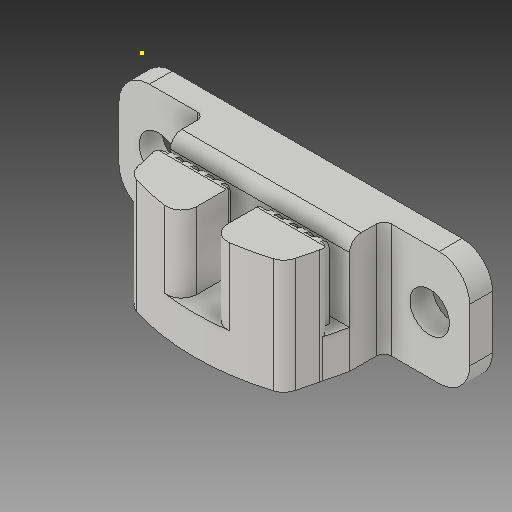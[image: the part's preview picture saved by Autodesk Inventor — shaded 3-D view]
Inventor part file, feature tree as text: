
AUTODESK INVENTOR PART (.ipt)
format: ipt  version: 2017 (Build 210142000, 142)  size: 307,712 bytes
history: native  units: mm
features: sketch x12, other x3
ambient origin geometry x8: Origin, YZ Plane, XZ Plane, XY Plane, X Axis, Y Axis, Z Axis, Center Point
bodies: Solid1 (feature_tree)
feature tree (15):
  other  "X Belt Clamp_MIR.ipt"
  other  "Solid1::X Belt Clamp_MIR.ipt"
  other  "TaggingFeature1"
  sketch  "Sketch1"  dims[d0=10.0mm]
  sketch  "Sketch2"
  sketch  "Sketch3"
  sketch  "Sketch4"
  sketch  "Sketch5"
  sketch  "Sketch6"
  sketch  "Sketch7"
  sketch  "Sketch8"
  sketch  "Sketch9"
  sketch  "Sketch10"
  sketch  "Sketch11"
  sketch  "Sketch12"
